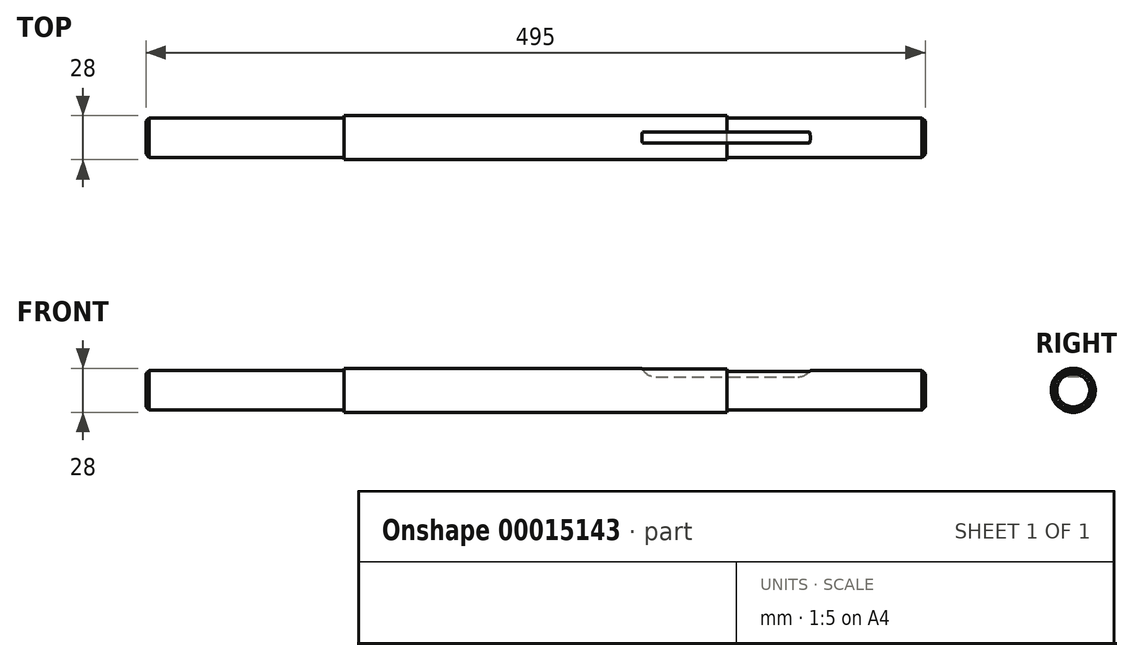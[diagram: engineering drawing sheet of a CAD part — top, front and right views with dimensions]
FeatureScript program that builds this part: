
annotation { "Feature Type Name" : "Feature", "Feature Type Description" : "" }
export const myFeature = defineFeature(function(context is Context, id is Id, definition is map)
    precondition{}
    {
        {
            var Q0;
            Q0=qCreatedBy(makeId("Right.planeOp"),FACE);
            var sketch = newSketch(context, id + "F0", { "sketchPlane" : qUnion([Q0])});
            skCircle(sketch, "E0", {"center": v(0, 0) * mm, "radius": 14 * mm});
            skCircle(sketch, "E1", {"center": v(0, 0) * mm, "radius": 12.5 * mm});
            skSolve(sketch);
        }
        {
            var Q0;
            Q0=makeQuery(id+"F0.imprint","IMPRINT",FACE,{"disambiguationData":[TD([[makeQuery(id+"F0.imprint","IMPRINT",EDGE,{"derivedFrom":sQuery(id+"F0.wireOp",EDGE,"E1")}),1.0]])]});
            extrude(context, id + "F1", {"entities" : qUnion([Q0]), "depth" : 126 * mm});
        }
        {
            var Q0;
            Q0=makeQuery(id+"F0.imprint","IMPRINT",FACE,{"disambiguationData":[TD([[makeQuery(id+"F0.imprint","IMPRINT",EDGE,{"derivedFrom":sQuery(id+"F0.wireOp",EDGE,"E1")}),1.0]])]});
            var Q1;
            Q1=makeQuery(id+"F0.imprint","IMPRINT",FACE,{"disambiguationData":[TD([[makeQuery(id+"F0.imprint","IMPRINT",EDGE,{"derivedFrom":sQuery(id+"F0.wireOp",EDGE,"E0")}),1.0]])]});
            extrude(context, id + "F2", {"entities" : qUnion([Q0, Q1]), "operationType" : NewBodyOperationType.ADD, "oppositeDirection" : true, "depth" : 243 * mm});
        }
        {
            var Q0;
            Q0=makeQuery(id+"F2.opExtrude","CAP_FACE",FACE,{"disambiguationData":[OSD([sQuery(id+"F0.wireOp",EDGE,"E0")])],"isStart":false});
            var sketch = newSketch(context, id + "F3", { "sketchPlane" : qUnion([Q0])});
            skCircle(sketch, "E2.0", {"center": v(0, 0) * mm, "radius": 14 * mm});
            skCircle(sketch, "E3", {"center": v(0, 0) * mm, "radius": 12.5 * mm});
            skSolve(sketch);
        }
        {
            var Q0;
            Q0=makeQuery(id+"F3.imprint","IMPRINT",FACE,{"disambiguationData":[TD([[makeQuery(id+"F3.imprint","IMPRINT",EDGE,{"derivedFrom":sQuery(id+"F3.wireOp",EDGE,"E3")}),1.0]])]});
            extrude(context, id + "F4", {"entities" : qUnion([Q0]), "operationType" : NewBodyOperationType.ADD, "depth" : 126 * mm});
        }
        {
            var Q0;
            Q0=qCreatedBy(makeId("Front.planeOp"),FACE);
            var sketch = newSketch(context, id + "F5", { "sketchPlane" : qUnion([Q0])});
            skLineSegment(sketch, "E4.bottom", {"start": v(-45, 17.86) * mm, "end": v(45, 17.86) * mm});
            skLineSegment(sketch, "E4.top", {"start": v(-45, 8.5) * mm, "end": v(45, 8.5) * mm});
            skLineSegment(sketch, "E4.left", {"start": v(-45, 17.86) * mm, "end": v(-45, 8.5) * mm, "construction": true});
            skLineSegment(sketch, "E4.right", {"start": v(45, 17.86) * mm, "end": v(45, 8.5) * mm, "construction": true});
            skLineSegment(sketch, "E5", {"start": v(0, 0) * mm, "end": v(0, 26.81) * mm, "construction": true});
            skLineSegment(sketch, "E6", {"start": v(0, 12.5) * mm, "end": v(126, 12.5) * mm, "construction": true});
            skArc(sketch, "E7", {"start": v(45, 8.5) * mm, "mid": v(49.47, 9.56) * mm, "end": v(53, 12.5) * mm});
            skArc(sketch, "E8.0.MirrorCS", {"start": v(-45, 8.5) * mm, "mid": v(-50.24, 9.99) * mm, "end": v(-53.93, 14) * mm});
            skPoint(sketch, "E9.orphan", {"position": v(-53, 12.5) * mm});
            skLineSegment(sketch, "E10", {"start": v(-243, 14) * mm, "end": v(0, 14) * mm, "construction": true});
            skLineSegment(sketch, "E11", {"start": v(-53.93, 14) * mm, "end": v(-53.93, 17.86) * mm});
            skLineSegment(sketch, "E12", {"start": v(-53.93, 17.86) * mm, "end": v(-45, 17.86) * mm});
            skLineSegment(sketch, "E13", {"start": v(53, 12.5) * mm, "end": v(53, 17.86) * mm});
            skLineSegment(sketch, "E14", {"start": v(53, 17.86) * mm, "end": v(45, 17.86) * mm});
            skSolve(sketch);
        }
        {
            var Q0;
            Q0=makeQuery(id+"F5.imprint","IMPRINT",FACE,{"disambiguationData":[TD([[makeQuery(id+"F5.imprint","IMPRINT",EDGE,{"derivedFrom":sQuery(id+"F5.wireOp",EDGE,"E4.bottom")}),-1.0]])]});
            extrude(context, id + "F6", {"entities" : qUnion([Q0]), "operationType" : NewBodyOperationType.REMOVE, "endBound" : BoundingType.SYMMETRIC, "oppositeDirection" : true, "depth" : 7 * mm});
        }
        {
            var Q0;
            Q0=makeQuery(id+"F1.opExtrude","CAP_EDGE",EDGE,{"disambiguationData":[OSD([sQuery(id+"F0.wireOp",EDGE,"E1")])],"isStart":false});
            var Q1;
            Q1=makeQuery(id+"F4.opExtrude","CAP_EDGE",EDGE,{"disambiguationData":[OSD([sQuery(id+"F3.wireOp",EDGE,"E3")])],"isStart":false});
            chamfer(context, id + "F7", {"entities" : qUnion([Q0, Q1]), "width" : 2 * mm, "tangentPropagation" : true});
        }
    });
